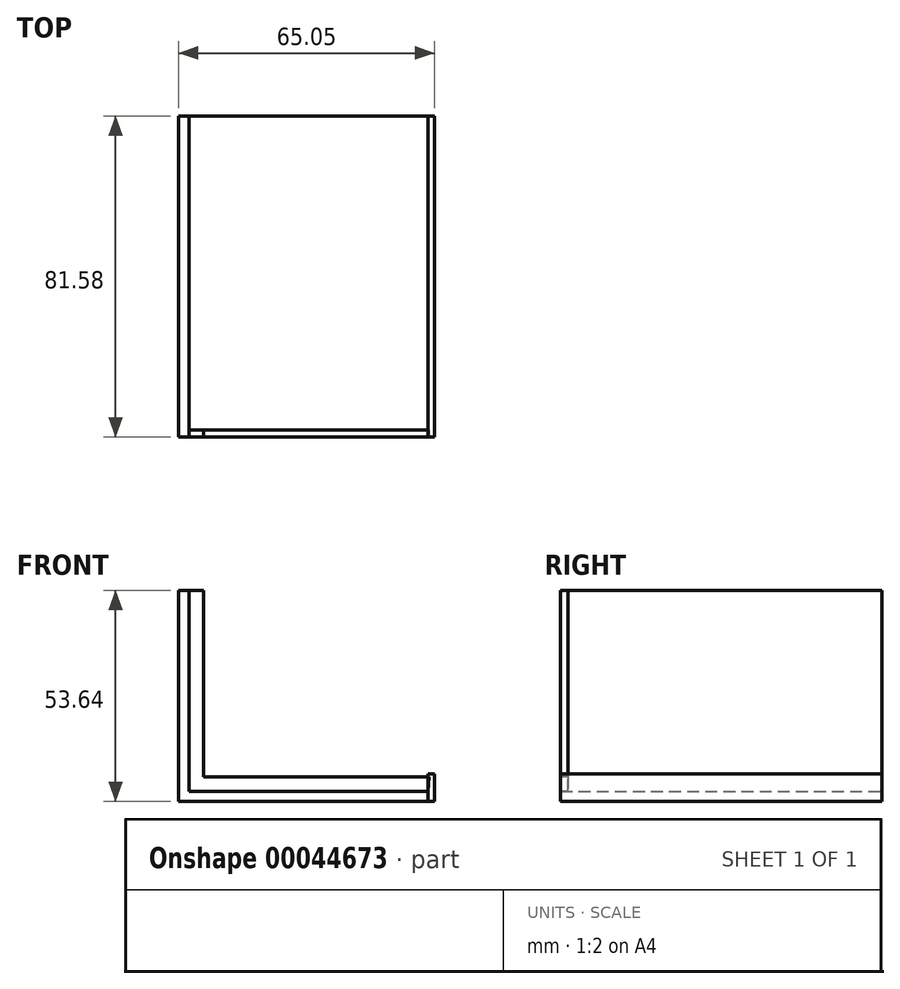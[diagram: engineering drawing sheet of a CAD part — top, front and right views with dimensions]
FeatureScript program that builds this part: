
annotation { "Feature Type Name" : "Feature", "Feature Type Description" : "" }
export const myFeature = defineFeature(function(context is Context, id is Id, definition is map)
    precondition{}
    {
        {
            var Q0;
            Q0=qCreatedBy(makeId("Front.planeOp"),FACE);
            var sketch = newSketch(context, id + "F0", { "sketchPlane" : qUnion([Q0])});
            skLineSegment(sketch, "E0", {"start": v(-46.5, 31.85) * mm, "end": v(-46.5, -21.8) * mm});
            skLineSegment(sketch, "E1", {"start": v(-46.5, -21.8) * mm, "end": v(16.88, -21.8) * mm});
            skLineSegment(sketch, "E2", {"start": v(16.88, -21.8) * mm, "end": v(16.88, -19.15) * mm});
            skLineSegment(sketch, "E3", {"start": v(16.88, -19.15) * mm, "end": v(-43.85, -19.15) * mm});
            skLineSegment(sketch, "E4", {"start": v(-43.85, -19.15) * mm, "end": v(-43.85, 31.85) * mm});
            skLineSegment(sketch, "E5", {"start": v(-43.85, 31.85) * mm, "end": v(-46.5, 31.85) * mm});
            skSolve(sketch);
        }
        {
            var Q0;
            Q0=makeQuery(id+"F0.imprint","IMPRINT",FACE,{"disambiguationData":[TD([[makeQuery(id+"F0.imprint","IMPRINT",EDGE,{"derivedFrom":sQuery(id+"F0.wireOp",EDGE,"E0")}),1.0]])]});
            extrude(context, id + "F1", {"entities" : qUnion([Q0]), "depth" : 81.58 * mm});
        }
        {
            var Q0;
            Q0=makeQuery(id+"F1.opExtrude","CAP_FACE",FACE,{"disambiguationData":[OSD([sQuery(id+"F0.wireOp",EDGE,"E0"),sQuery(id+"F0.wireOp",EDGE,"E1"),sQuery(id+"F0.wireOp",EDGE,"E2"),sQuery(id+"F0.wireOp",EDGE,"E3"),sQuery(id+"F0.wireOp",EDGE,"E4"),sQuery(id+"F0.wireOp",EDGE,"E5")])],"isStart":false});
            var sketch = newSketch(context, id + "F2", { "sketchPlane" : qUnion([Q0])});
            skLineSegment(sketch, "E6", {"start": v(-43.85, 31.85) * mm, "end": v(-40.2, 31.85) * mm});
            skLineSegment(sketch, "E7", {"start": v(-40.2, 31.85) * mm, "end": v(-40.2, -19.15) * mm});
            skLineSegment(sketch, "E8", {"start": v(-40.2, -19.15) * mm, "end": v(-43.85, -19.15) * mm});
            skLineSegment(sketch, "E9", {"start": v(-43.85, -19.15) * mm, "end": v(-43.85, -15.5) * mm});
            skLineSegment(sketch, "E10", {"start": v(-43.85, -15.5) * mm, "end": v(17.08, -15.5) * mm});
            skLineSegment(sketch, "E11", {"start": v(17.08, -15.5) * mm, "end": v(16.88, -19.15) * mm});
            skSolve(sketch);
        }
        {
            var Q0;
            {var subQ3=sQuery(id+"F2.wireOp",EDGE,"E6");Q0=makeQuery(id+"F2.imprint","IMPRINT",FACE,{"disambiguationData":[TD([[makeQuery(id+"F2.imprint","IMPRINT",EDGE,{"derivedFrom":subQ3}),-1.0]])]});}
            var Q1;
            {var subQ0=sQuery(id+"F2.wireOp",EDGE,"E11");Q1=makeQuery(id+"F2.imprint","IMPRINT",FACE,{"disambiguationData":[TD([[makeQuery(id+"F2.imprint","IMPRINT",EDGE,{"derivedFrom":subQ0}),-1.0]])]});}
            var Q2;
            {var subQ4=sQuery(id+"F2.wireOp",EDGE,"E8");Q2=makeQuery(id+"F2.imprint","IMPRINT",FACE,{"disambiguationData":[TD([[makeQuery(id+"F2.imprint","IMPRINT",EDGE,{"derivedFrom":subQ4}),-1.0]])]});}
            extrude(context, id + "F3", {"entities" : qUnion([Q0, Q1, Q2]), "oppositeDirection" : true, "depth" : 1.83 * mm});
        }
        {
            var Q0;
            Q0=makeQuery(id+"F1.opExtrude","SWEPT_FACE",FACE,{"disambiguationData":[OSD([sQuery(id+"F0.wireOp",EDGE,"E4")])]});
            var sketch = newSketch(context, id + "F4", { "sketchPlane" : qUnion([Q0])});
            skLineSegment(sketch, "E12", {"start": v(-81.58, -12.06) * mm, "end": v(0, -12.06) * mm});
            skLineSegment(sketch, "E13", {"start": v(0, -12.06) * mm, "end": v(0, -21.8) * mm});
            skLineSegment(sketch, "E14", {"start": v(0, -21.8) * mm, "end": v(-81.58, -21.8) * mm});
            skLineSegment(sketch, "E15", {"start": v(-81.58, -21.8) * mm, "end": v(-81.58, -12.06) * mm});
            skSolve(sketch);
        }
        {
            var Q0;
            Q0=makeQuery(id+"F1.opExtrude","SWEPT_FACE",FACE,{"disambiguationData":[OSD([sQuery(id+"F0.wireOp",EDGE,"E2")])]});
            var sketch = newSketch(context, id + "F5", { "sketchPlane" : qUnion([Q0])});
            skLineSegment(sketch, "E16", {"start": v(-81.58, -14.73) * mm, "end": v(0, -14.73) * mm});
            skLineSegment(sketch, "E17", {"start": v(0, -14.73) * mm, "end": v(0, -21.8) * mm});
            skLineSegment(sketch, "E18", {"start": v(0, -21.8) * mm, "end": v(-81.58, -21.8) * mm});
            skLineSegment(sketch, "E19", {"start": v(-81.58, -21.8) * mm, "end": v(-81.58, -14.73) * mm});
            skSolve(sketch);
        }
        {
            var Q0;
            Q0 = qSketchRegion(id + "F5", true);
            extrude(context, id + "F6", {"entities" : qUnion([Q0]), "depth" : 1.68 * mm});
        }
    });
